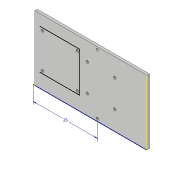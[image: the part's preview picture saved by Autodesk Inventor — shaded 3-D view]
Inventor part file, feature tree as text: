
AUTODESK INVENTOR PART (.ipt)
format: ipt  version: 2019 (Build 230136000, 136)  size: 177,152 bytes
history: native  units: in
note: dims shown in document units (in); Inventor stores cm internally (conversion verified against a paired STEP export)
features: sketch x16, extrude x8
ambient origin geometry x8: Origin, YZ Plane, XZ Plane, XY Plane, X Axis, Y Axis, Z Axis, Center Point
bodies: Solid1 (feature_tree)
feature tree (24):
  extrude  "Extrusion1"  Depth=10.2362in
  sketch  "Sketch2"  dims[d0=13.7795in d1=10.2362in]
  sketch  "Sketch3"  dims[d2=0.3937in d3=0.0in d4=1.7717in]
  sketch  "Sketch4"  dims[d5=1.7717in d6=0.7874in]
  sketch  "Sketch5"  dims[d7=0.7874in d8=7.0866in]
  extrude  "Extrusion2"  Depth=0.3937in
  sketch  "Sketch7"  dims[d11=6.2992in d12=0.3937in]
  extrude  "Extrusion3"  Depth=0.7874in
  sketch  "Sketch9"  dims[d15=5.5118in d16=5.5118in]
  extrude  "Extrusion4"  Depth=7.0866in
  extrude  "Extrusion5"  Depth=6.2992in
  sketch  "Sketch12"  dims[d19=0.3937in]
  sketch  "Sketch13"  dims[d20=0.3937in]
  extrude  "Extrusion6"  Depth=0.3937in
  extrude  "Extrusion7"  Depth=5.5118in
  sketch  "Sketch16"  dims[d24=6.2992in]
  extrude  "Extrusion8"  Depth=5.5118in
  sketch  "Sketch6"  dims[d9=6.2992in d10=6.2992in]
  sketch  "Sketch8"  dims[d13=5.9055in d14=5.5118in]
  sketch  "Sketch10"  dims[d17=0.3937in]
  sketch  "Sketch11"  dims[d18=0.3937in]
  sketch  "Sketch14"  dims[d21=0.0in d22=0.0in]
  sketch  "Sketch15"  dims[d23=0.7874in]
  sketch  "Sketch17"  dims[d29=0.3937in d36=0.3937in d37=0.0in d45=0.9843in d59=4.7244in d60=4.7244in d61=0.3937in d62=0.3937in d63=0.3937in d64=0.3937in d65=4.7244in d66=4.7244in d67=0.3937in d68=0.3937in d69=0.3937in d70=0.3937in d71=4.3307in d72=4.3307in d73=0.3937in d74=0.3937in d75=0.3937in d76=0.3937in d77=0.0in d78=0.0in d79=3.937in d80=0.3937in d81=0.0in d84=0.3937in d85=0.0in d87=0.3937in d88=0.0in d89=0.3937in d90=0.3937in d91=0.3937in d92=0.3937in d93=10.2362in d94=0.3937in d95=9.4488in d96=0.3937in d97=0.3937in d98=0.3937in d99=0.0in]
